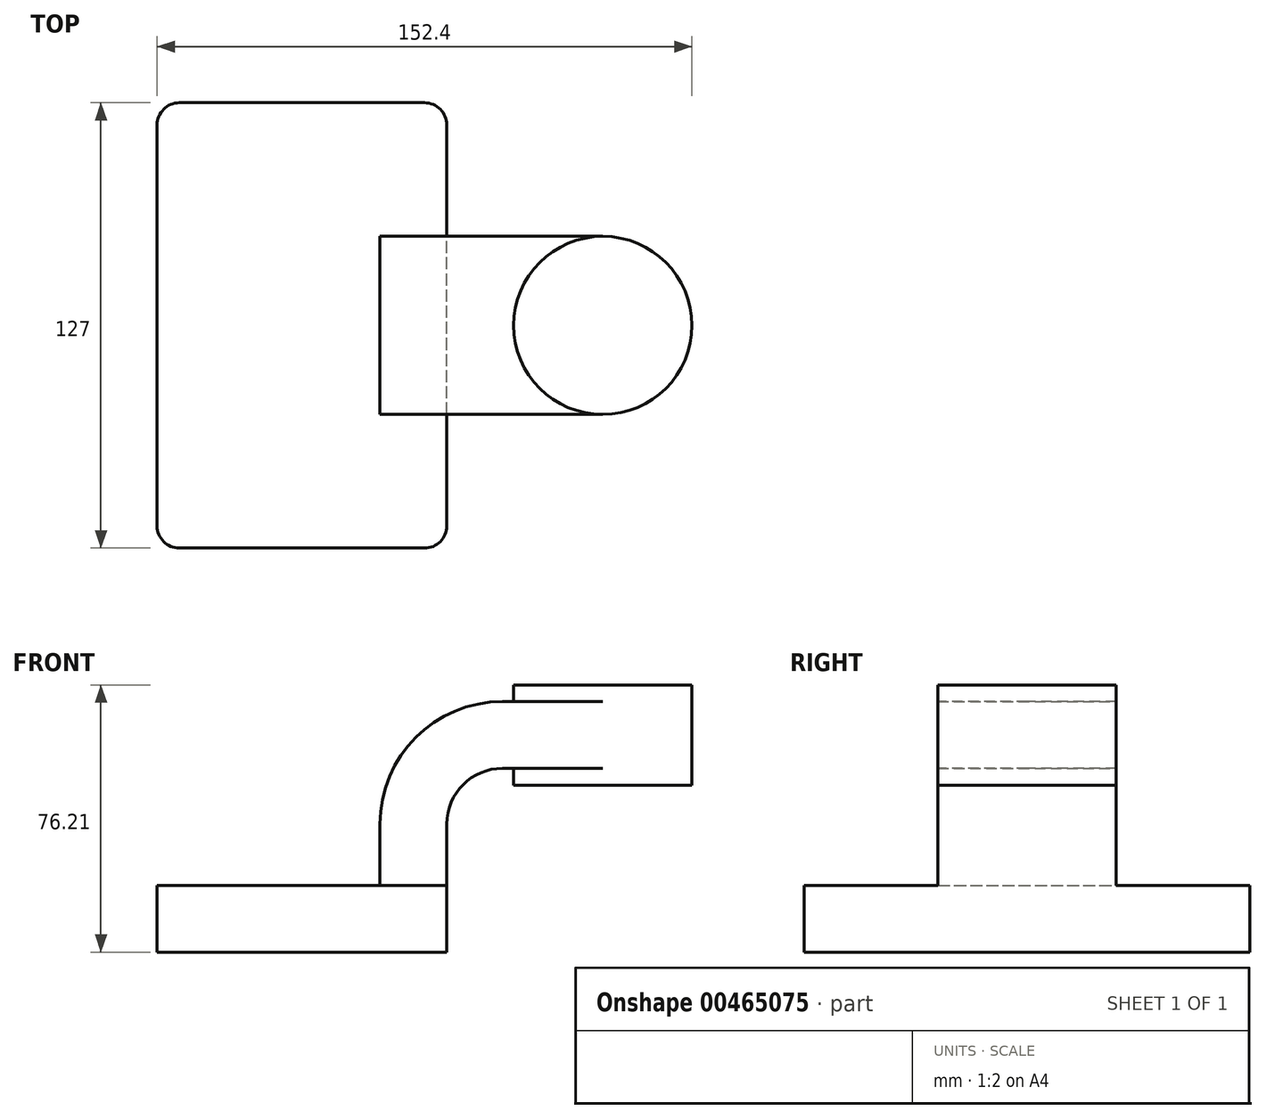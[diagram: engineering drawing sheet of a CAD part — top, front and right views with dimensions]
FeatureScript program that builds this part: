
annotation { "Feature Type Name" : "Feature", "Feature Type Description" : "" }
export const myFeature = defineFeature(function(context is Context, id is Id, definition is map)
    precondition{}
    {
        {
            var Q0;
            Q0=qCreatedBy(makeId("Front.planeOp"),FACE);
            var sketch = newSketch(context, id + "F0", { "sketchPlane" : qUnion([Q0])});
            skLineSegment(sketch, "E0.bottom", {"start": v(-41.28, -9.53) * mm, "end": v(41.28, -9.53) * mm});
            skLineSegment(sketch, "E0.top", {"start": v(-41.28, 9.53) * mm, "end": v(41.28, 9.53) * mm});
            skLineSegment(sketch, "E0.left", {"start": v(-41.28, -9.53) * mm, "end": v(-41.28, 9.53) * mm});
            skLineSegment(sketch, "E0.right", {"start": v(41.28, -9.53) * mm, "end": v(41.28, 9.53) * mm});
            skPoint(sketch, "E0.middle", {"position": v(0, 0) * mm});
            skLineSegment(sketch, "E1", {"start": v(41.28, 9.53) * mm, "end": v(41.28, 27) * mm});
            skLineSegment(sketch, "E2.bottom", {"start": v(111.13, 38.1) * mm, "end": v(60.33, 38.1) * mm});
            skLineSegment(sketch, "E2.top", {"start": v(111.13, 66.67) * mm, "end": v(60.33, 66.67) * mm});
            skLineSegment(sketch, "E2.left", {"start": v(111.13, 38.1) * mm, "end": v(111.13, 66.67) * mm});
            skLineSegment(sketch, "E2.right", {"start": v(60.33, 38.1) * mm, "end": v(60.33, 66.67) * mm});
            skPoint(sketch, "E2.middle", {"position": v(85.73, 52.39) * mm});
            skArc(sketch, "E3", {"start": v(41.28, 27) * mm, "mid": v(45.92, 38.23) * mm, "end": v(57.15, 42.88) * mm});
            skLineSegment(sketch, "E4", {"start": v(57.15, 42.88) * mm, "end": v(85.73, 42.88) * mm});
            skLineSegment(sketch, "E5.0", {"start": v(57.15, 61.93) * mm, "end": v(85.73, 61.93) * mm});
            skArc(sketch, "E5.1", {"start": v(22.23, 27) * mm, "mid": v(32.45, 51.7) * mm, "end": v(57.15, 61.93) * mm});
            skLineSegment(sketch, "E5.2", {"start": v(22.23, 9.53) * mm, "end": v(22.23, 27) * mm});
            skLineSegment(sketch, "E6", {"start": v(85.73, 38.1) * mm, "end": v(85.73, 66.67) * mm});
            skFitSpline(sketch, "E7", {"points": [v(-41.28, 9.53) * mm, v(57.15, 61.93) * mm], "startDerivative": vector(27.83, 130.95) * mm, "endDerivative": vector(137.65, -8.9) * mm});
            skSolve(sketch);
        }
        {
            var Q0;
            Q0=makeQuery(id+"F0.imprint","IMPRINT",FACE,{"disambiguationData":[TD([[makeQuery(id+"F0.imprint","IMPRINT",EDGE,{"derivedFrom":sQuery(id+"F0.wireOp",EDGE,"E0.bottom")}),1.0]])]});
            extrude(context, id + "F1", {"entities" : qUnion([Q0]), "endBound" : BoundingType.SYMMETRIC, "depth" : 127 * mm});
        }
        {
            var Q0;
            {var subQ1=sQuery(id+"F0.wireOp",EDGE,"E1");Q0=makeQuery(id+"F0.imprint","IMPRINT",FACE,{"disambiguationData":[TD([[makeQuery(id+"F0.imprint","IMPRINT",EDGE,{"derivedFrom":subQ1}),1.0]])]});}
            var Q1;
            {var subQ0=sQuery(id+"F0.wireOp",EDGE,"E4");var subQ1=sQuery(id+"F0.wireOp",EDGE,"E2.right");var subQ2=makeQuery(id+"F0.imprint","INTERSECT",VERTEX,{"derivedFrom":[subQ1,subQ0]});Q1=makeQuery(id+"F0.imprint","IMPRINT",FACE,{"disambiguationData":[TD([[makeQuery(id+"F0.imprint","IMPRINT",EDGE,{"disambiguationData":[TD([[subQ2,-1.0]])],"derivedFrom":subQ1}),-1.0]])]});}
            extrude(context, id + "F2", {"entities" : qUnion([Q0, Q1]), "operationType" : NewBodyOperationType.ADD, "endBound" : BoundingType.SYMMETRIC, "depth" : 50.8 * mm});
        }
        {
            var Q0;
            Q0=makeQuery(id+"F0.imprint","IMPRINT",FACE,{"disambiguationData":[TD([[makeQuery(id+"F0.imprint","IMPRINT",EDGE,{"derivedFrom":sQuery(id+"F0.wireOp",EDGE,"E5.1")}),1.0]])]});
            extrude(context, id + "F3", {"entities" : qUnion([Q0]), "operationType" : NewBodyOperationType.ADD, "endBound" : BoundingType.SYMMETRIC, "depth" : 15.88 * mm});
        }
        {
            var Q0;
            {var subQ0=sQuery(id+"F0.wireOp",EDGE,"E2.left");Q0=makeQuery(id+"F0.imprint","IMPRINT",FACE,{"disambiguationData":[TD([[makeQuery(id+"F0.imprint","IMPRINT",EDGE,{"derivedFrom":subQ0}),1.0]])]});}
            var Q1;
            Q1=sQuery(id+"F0.wireOp",EDGE,"E6");
            revolve(context, id + "F4", {"operationType" : NewBodyOperationType.ADD, "entities" : qUnion([Q0]), "axis" : qUnion([Q1]), "revolveType" : RevolveType.FULL});
        }
        {
            var Q0;
            Q0=makeQuery(id+"F1.opExtrude","CAP_EDGE",EDGE,{"disambiguationData":[OSD([sQuery(id+"F0.wireOp",EDGE,"E0.right")])],"isStart":false});
            var Q1;
            Q1=makeQuery(id+"F1.opExtrude","CAP_EDGE",EDGE,{"disambiguationData":[OSD([sQuery(id+"F0.wireOp",EDGE,"E0.left")])],"isStart":false});
            var Q2;
            Q2=makeQuery(id+"F1.opExtrude","CAP_EDGE",EDGE,{"disambiguationData":[OSD([sQuery(id+"F0.wireOp",EDGE,"E0.right")])],"isStart":true});
            var Q3;
            Q3=makeQuery(id+"F1.opExtrude","CAP_EDGE",EDGE,{"disambiguationData":[OSD([sQuery(id+"F0.wireOp",EDGE,"E0.left")])],"isStart":true});
            fillet(context, id + "F5", {"entities" : qUnion([Q0, Q1, Q2, Q3]), "radius" : 6.35 * mm, "tangentPropagation" : true, "allowEdgeOverflow" : false});
        }
    });
